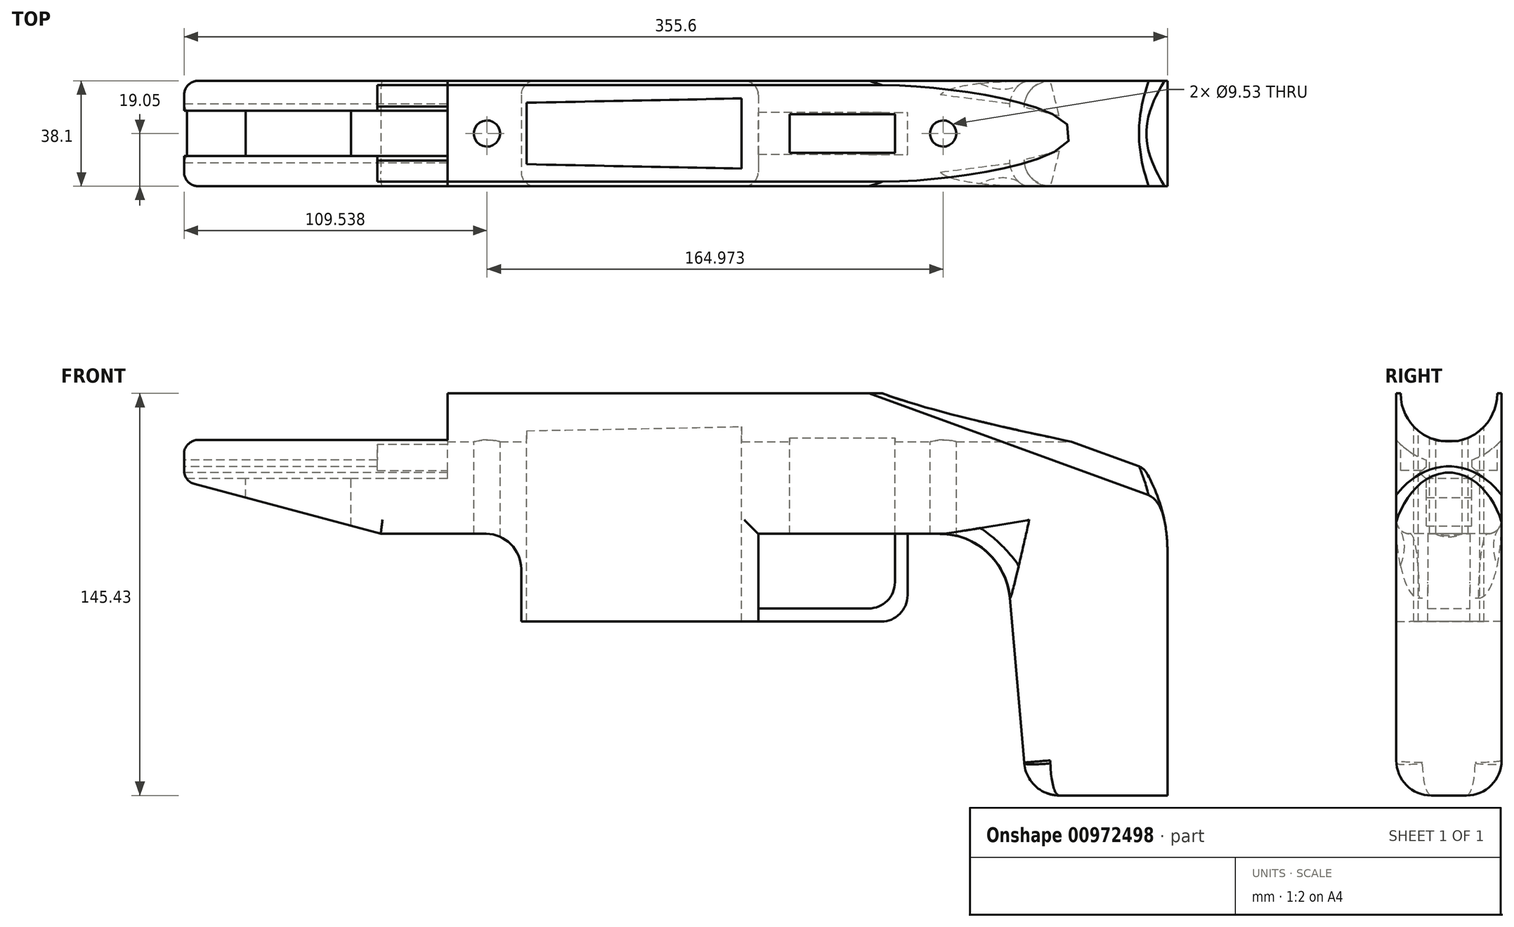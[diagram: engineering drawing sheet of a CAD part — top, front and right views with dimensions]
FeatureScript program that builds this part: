
annotation { "Feature Type Name" : "Feature", "Feature Type Description" : "" }
export const myFeature = defineFeature(function(context is Context, id is Id, definition is map)
    precondition{}
    {
        {
            var Q0;
            Q0=qCreatedBy(makeId("Front.planeOp"),FACE);
            var sketch = newSketch(context, id + "F0", { "sketchPlane" : qUnion([Q0])});
            skLineSegment(sketch, "E0", {"start": v(177.8, -57.15) * mm, "end": v(177.8, -145.43) * mm});
            skLineSegment(sketch, "E1", {"start": v(177.8, -145.43) * mm, "end": v(127, -145.43) * mm});
            skLineSegment(sketch, "E2", {"start": v(127, -145.43) * mm, "end": v(118.72, -50.8) * mm});
            skLineSegment(sketch, "E3", {"start": v(118.72, -50.8) * mm, "end": v(29.82, -50.8) * mm});
            skLineSegment(sketch, "E4", {"start": v(29.82, -50.8) * mm, "end": v(29.82, -82.55) * mm});
            skLineSegment(sketch, "E5", {"start": v(29.82, -82.55) * mm, "end": v(-55.9, -82.55) * mm});
            skLineSegment(sketch, "E6", {"start": v(-55.9, -82.55) * mm, "end": v(-55.9, -50.8) * mm});
            skLineSegment(sketch, "E7", {"start": v(-55.9, -50.8) * mm, "end": v(-106.7, -50.8) * mm});
            skLineSegment(sketch, "E8", {"start": v(-106.7, -50.8) * mm, "end": v(-177.8, -31.75) * mm});
            skLineSegment(sketch, "E9", {"start": v(-177.8, -31.75) * mm, "end": v(-177.8, -9.53) * mm});
            skLineSegment(sketch, "E10", {"start": v(-107.95, -9.53) * mm, "end": v(-107.95, 0) * mm});
            skLineSegment(sketch, "E11", {"start": v(-107.95, 0) * mm, "end": v(120.65, 0) * mm});
            skLineSegment(sketch, "E12", {"start": v(-107.95, -9.53) * mm, "end": v(-177.8, -9.53) * mm});
            skArc(sketch, "E13", {"start": v(177.8, -57.15) * mm, "mid": v(161.06, -16.74) * mm, "end": v(120.65, 0) * mm});
            skLineSegment(sketch, "E14", {"start": v(0, 57.34) * mm, "end": v(0, -146.77) * mm, "construction": true});
            skSolve(sketch);
        }
        {
            var Q0;
            Q0=makeQuery(id+"F0.imprint","IMPRINT",FACE,{"disambiguationData":[TD([[makeQuery(id+"F0.imprint","IMPRINT",EDGE,{"derivedFrom":sQuery(id+"F0.wireOp",EDGE,"E0")}),-1.0]])]});
            extrude(context, id + "F1", {"entities" : qUnion([Q0]), "oppositeDirection" : true, "depth" : 19.05 * mm, "offsetDistance" : 25.4 * mm, "hasSecondDirection" : true, "secondDirectionOppositeDirection" : false, "secondDirectionDepth" : 19.05 * mm});
        }
        {
            var Q0;
            Q0=makeQuery(id+"F1.opExtrude","CAP_EDGE",EDGE,{"disambiguationData":[OSD([sQuery(id+"F0.wireOp",EDGE,"E2")])],"isStart":true});
            var Q1;
            Q1=makeQuery(id+"F1.opExtrude","CAP_EDGE",EDGE,{"disambiguationData":[OSD([sQuery(id+"F0.wireOp",EDGE,"E2")])],"isStart":false});
            fillet(context, id + "F2", {"entities" : qUnion([Q0, Q1]), "radius" : 9.52 * mm, "tangentPropagation" : true, "allowEdgeOverflow" : false});
        }
        {
            var Q0;
            Q0=makeQuery(id+"F1.opExtrude","CAP_EDGE",EDGE,{"disambiguationData":[OSD([sQuery(id+"F0.wireOp",EDGE,"E1")])],"isStart":false});
            fillet(context, id + "F3", {"entities" : qUnion([Q0]), "radius" : 12.7 * mm, "tangentPropagation" : true, "allowEdgeOverflow" : false});
        }
        {
            var Q0;
            Q0=makeQuery(id+"F1.opExtrude","SWEPT_EDGE",EDGE,{"disambiguationData":[OSD([sQuery(id+"F0.wireOp",EDGE,"E6"),sQuery(id+"F0.wireOp",EDGE,"E7")])]});
            fillet(context, id + "F4", {"entities" : qUnion([Q0]), "radius" : 12.7 * mm, "tangentPropagation" : true, "allowEdgeOverflow" : false});
        }
        {
            var Q0;
            Q0=makeQuery(id+"F1.opExtrude","CAP_EDGE",EDGE,{"disambiguationData":[OSD([sQuery(id+"F0.wireOp",EDGE,"E3")])],"isStart":true});
            var Q1;
            Q1=makeQuery(id+"F1.opExtrude","CAP_EDGE",EDGE,{"disambiguationData":[OSD([sQuery(id+"F0.wireOp",EDGE,"E4")])],"isStart":true});
            var Q2;
            Q2=makeQuery(id+"F1.opExtrude","CAP_EDGE",EDGE,{"disambiguationData":[OSD([sQuery(id+"F0.wireOp",EDGE,"E6")])],"isStart":true});
            var Q3;
            Q3=makeQuery(id+"F1.opExtrude","CAP_EDGE",EDGE,{"disambiguationData":[OSD([sQuery(id+"F0.wireOp",EDGE,"E8")])],"isStart":true});
            var Q4;
            Q4=makeQuery(id+"F1.opExtrude","CAP_EDGE",EDGE,{"disambiguationData":[OSD([sQuery(id+"F0.wireOp",EDGE,"E3")])],"isStart":false});
            var Q5;
            Q5=makeQuery(id+"F1.opExtrude","CAP_EDGE",EDGE,{"disambiguationData":[OSD([sQuery(id+"F0.wireOp",EDGE,"E6")])],"isStart":false});
            var Q6;
            Q6=makeQuery(id+"F1.opExtrude","CAP_EDGE",EDGE,{"disambiguationData":[OSD([sQuery(id+"F0.wireOp",EDGE,"E8")])],"isStart":false});
            var Q7;
            Q7=makeQuery(id+"F1.opExtrude","CAP_EDGE",EDGE,{"disambiguationData":[OSD([sQuery(id+"F0.wireOp",EDGE,"E4")])],"isStart":false});
            fillet(context, id + "F5", {"entities" : qUnion([Q0, Q1, Q2, Q3, Q4, Q5, Q6, Q7]), "radius" : 5.08 * mm, "tangentPropagation" : true, "allowEdgeOverflow" : false});
        }
        {
            var Q0;
            Q0=makeQuery(id+"F1.opExtrude","CAP_EDGE",EDGE,{"disambiguationData":[OSD([sQuery(id+"F0.wireOp",EDGE,"E9")])],"isStart":false});
            fillet(context, id + "F6", {"entities" : qUnion([Q0]), "radius" : 5.08 * mm, "tangentPropagation" : true, "allowEdgeOverflow" : false});
        }
        {
            var Q0;
            Q0=qCreatedBy(makeId("Right.planeOp"),FACE);
            var sketch = newSketch(context, id + "F7", { "sketchPlane" : qUnion([Q0])});
            skCircle(sketch, "E15", {"center": v(0, 0) * mm, "radius": 17.46 * mm});
            skSolve(sketch);
        }
        {
            var Q0;
            Q0=makeQuery(id+"F7.imprint","IMPRINT",FACE,{"disambiguationData":[TD([[makeQuery(id+"F7.imprint","IMPRINT",EDGE,{"derivedFrom":sQuery(id+"F7.wireOp",EDGE,"E15")}),1.0]])]});
            extrude(context, id + "F8", {"entities" : qUnion([Q0]), "operationType" : NewBodyOperationType.REMOVE, "endBound" : BoundingType.THROUGH_ALL, "oppositeDirection" : true, "depth" : 25.4 * mm, "offsetDistance" : 25.4 * mm, "hasSecondDirection" : true, "secondDirectionBound" : SecondDirectionBoundingType.THROUGH_ALL, "secondDirectionOppositeDirection" : false, "secondDirectionDepth" : 25.4 * mm});
        }
        {
            var Q0;
            Q0=makeQuery(id+"F1.opExtrude","SWEPT_FACE",FACE,{"disambiguationData":[OSD([sQuery(id+"F0.wireOp",EDGE,"E9")])]});
            var sketch = newSketch(context, id + "F9", { "sketchPlane" : qUnion([Q0])});
            skLineSegment(sketch, "E16", {"start": v(0, 0) * mm, "end": v(0, -58.85) * mm, "construction": true});
            skPoint(sketch, "E16.endSnap0", {"position": v(0, -27.85) * mm});
            skLineSegment(sketch, "E17", {"start": v(-8.2, -24.04) * mm, "end": v(-8.2, -26.54) * mm});
            skLineSegment(sketch, "E18", {"start": v(-8.2, -26.54) * mm, "end": v(-10.67, -28.7) * mm});
            skLineSegment(sketch, "E19", {"start": v(-10.67, -28.7) * mm, "end": v(-8.2, -30.86) * mm});
            skLineSegment(sketch, "E20", {"start": v(-8.2, -30.86) * mm, "end": v(8.2, -30.86) * mm});
            skLineSegment(sketch, "E21", {"start": v(8.2, -30.86) * mm, "end": v(10.67, -28.7) * mm});
            skLineSegment(sketch, "E22", {"start": v(10.67, -28.7) * mm, "end": v(8.2, -26.54) * mm});
            skLineSegment(sketch, "E23", {"start": v(8.2, -26.54) * mm, "end": v(8.2, -24.04) * mm});
            skLineSegment(sketch, "E24", {"start": v(-10.67, -28.7) * mm, "end": v(10.67, -28.7) * mm, "construction": true});
            skArc(sketch, "E25", {"start": v(8.2, -24.04) * mm, "mid": v(0, 25.4) * mm, "end": v(-8.2, -24.04) * mm});
            skPoint(sketch, "E26.orphan", {"position": v(-8.2, -10.48) * mm});
            skPoint(sketch, "E27.orphan", {"position": v(8.2, -10.48) * mm});
            skSolve(sketch);
        }
        {
            var Q0;
            {var subQ11=sQuery(id+"F9.wireOp",EDGE,"E17");Q0=makeQuery(id+"F9.imprint","IMPRINT",FACE,{"disambiguationData":[TD([[makeQuery(id+"F9.imprint","IMPRINT",EDGE,{"derivedFrom":subQ11}),1.0]])]});}
            var Q1;
            {var subQ1=sQuery(id+"F0.wireOp",EDGE,"E9");var subQ2=makeQuery(id+"F1.opExtrude","SWEPT_FACE",FACE,{"disambiguationData":[OSD([subQ1])]});var subQ7=makeQuery(id+"F8.boolean.opBoolean","INTERSECT",EDGE,{"derivedFrom":[subQ2,makeQuery(id+"F8.opExtrude","SWEPT_FACE",FACE,{"disambiguationData":[OSD([sQuery(id+"F7.wireOp",EDGE,"E15")])]})]});Q1=makeQuery(id+"F9.imprint","IMPRINT",FACE,{"disambiguationData":[TD([[makeQuery(id+"F9.imprint","IMPRINT",EDGE,{"derivedFrom":subQ7}),-1.0]])]});}
            var Q2;
            {var subQ0=sQuery(id+"F0.wireOp",EDGE,"E12");var subQ1=sQuery(id+"F0.wireOp",EDGE,"E11");var subQ2=sQuery(id+"F0.wireOp",EDGE,"E10");Q2=makeQuery(id+"F8.boolean.opBoolean","SPLIT",FACE,{"disambiguationData":[TD([makeQuery(id+"F1.opExtrude","CAP_FACE",FACE,{"disambiguationData":[OSD([sQuery(id+"F0.wireOp",EDGE,"E0"),sQuery(id+"F0.wireOp",EDGE,"E1"),sQuery(id+"F0.wireOp",EDGE,"E2"),sQuery(id+"F0.wireOp",EDGE,"E3"),sQuery(id+"F0.wireOp",EDGE,"E4"),sQuery(id+"F0.wireOp",EDGE,"E5"),sQuery(id+"F0.wireOp",EDGE,"E6"),sQuery(id+"F0.wireOp",EDGE,"E7"),sQuery(id+"F0.wireOp",EDGE,"E8"),sQuery(id+"F0.wireOp",EDGE,"E9"),subQ2,subQ1,subQ0,sQuery(id+"F0.wireOp",EDGE,"E13")])],"isStart":true})])],"derivedFrom":makeQuery(id+"F1.opExtrude","SWEPT_FACE",FACE,{"disambiguationData":[OSD([subQ2])]})});}
            extrude(context, id + "F10", {"entities" : qUnion([Q0, Q1]), "operationType" : NewBodyOperationType.REMOVE, "endBound" : BoundingType.UP_TO_SURFACE, "oppositeDirection" : true, "depth" : 25.4 * mm, "endBoundEntityFace" : qUnion([Q2]), "offsetDistance" : 25.4 * mm});
        }
        {
            var Q0;
            Q0=qCreatedBy(makeId("Top.planeOp"),FACE);
            var sketch = newSketch(context, id + "F11", { "sketchPlane" : qUnion([Q0])});
            skPoint(sketch, "E28.0", {"position": v(-107.95, 0) * mm});
            skLineSegment(sketch, "E29", {"start": v(-107.95, 0) * mm, "end": v(-78.77, 0) * mm, "construction": true});
            skCircle(sketch, "E30", {"center": v(-68.26, 0) * mm, "radius": 4.76 * mm});
            skCircle(sketch, "E31", {"center": v(96.71, 0) * mm, "radius": 4.76 * mm});
            skSolve(sketch);
        }
        {
            var Q0;
            Q0=qSketchRegion(id+"F11",true);
            extrude(context, id + "F12", {"entities" : qUnion([Q0]), "operationType" : NewBodyOperationType.REMOVE, "endBound" : BoundingType.THROUGH_ALL, "oppositeDirection" : true, "depth" : 25.4 * mm, "offsetDistance" : 25.4 * mm});
        }
        {
            var Q0;
            Q0=makeQuery(id+"F1.opExtrude","SWEPT_EDGE",EDGE,{"disambiguationData":[OSD([sQuery(id+"F0.wireOp",EDGE,"E0"),sQuery(id+"F0.wireOp",EDGE,"E13")])]});
            cPlane(context, id + "F13", {"entities" : qUnion([Q0]), "cplaneType" : CPlaneType.LINE_ANGLE, "offset" : 25.4 * mm, "angle" : 110 * degree, "oppositeDirection" : true, "width" : 152.4 * mm, "height" : 152.4 * mm});
        }
        {
            var Q0;
            Q0=qCreatedBy(id+"F13.planeOp",FACE);
            var sketch = newSketch(context, id + "F14", { "sketchPlane" : qUnion([Q0])});
            skArc(sketch, "E32", {"start": v(19.05, 23.9) * mm, "mid": v(0, 32.5) * mm, "end": v(-19.05, 23.9) * mm});
            skLineSegment(sketch, "E33.0", {"start": v(19.05, 23.9) * mm, "end": v(19.05, 44.71) * mm});
            skLineSegment(sketch, "E34.0", {"start": v(-19.05, 23.9) * mm, "end": v(-19.05, 44.71) * mm});
            skLineSegment(sketch, "E35", {"start": v(19.05, 44.71) * mm, "end": v(-19.05, 44.71) * mm});
            skPoint(sketch, "E36.orphan", {"position": v(-19.05, 7.1) * mm});
            skPoint(sketch, "E37.0.end.orphan", {"position": v(19.05, 7.1) * mm});
            skSolve(sketch);
        }
        {
            var Q0;
            Q0=makeQuery(id+"F14.imprint","IMPRINT",FACE,{"disambiguationData":[TD([[makeQuery(id+"F14.imprint","IMPRINT",EDGE,{"derivedFrom":sQuery(id+"F14.wireOp",EDGE,"E32")}),-1.0]])]});
            extrude(context, id + "F15", {"entities" : qUnion([Q0]), "operationType" : NewBodyOperationType.REMOVE, "endBound" : BoundingType.THROUGH_ALL, "depth" : 25.4 * mm, "offsetDistance" : 25.4 * mm});
        }
        {
            var Q0;
            Q0=makeQuery(id+"F15.boolean.opBoolean","INTERSECT",EDGE,{"derivedFrom":[makeQuery(id+"F1.opExtrude","SWEPT_FACE",FACE,{"disambiguationData":[OSD([sQuery(id+"F0.wireOp",EDGE,"E13")])]}),makeQuery(id+"F15.opExtrude","SWEPT_FACE",FACE,{"disambiguationData":[OSD([sQuery(id+"F14.wireOp",EDGE,"E32")])]})]});
            fillet(context, id + "F16", {"entities" : qUnion([Q0]), "radius" : 5.08 * mm, "tangentPropagation" : true, "allowEdgeOverflow" : false});
        }
        {
            var Q0;
            Q0=qCreatedBy(makeId("Top.planeOp"),FACE);
            var sketch = newSketch(context, id + "F17", { "sketchPlane" : qUnion([Q0])});
            skLineSegment(sketch, "E38.0", {"start": v(-107.95, 17.46) * mm, "end": v(-107.95, -17.46) * mm});
            skLineSegment(sketch, "E39.0", {"start": v(-107.95, 17.46) * mm, "end": v(-82.55, 17.46) * mm});
            skLineSegment(sketch, "E40.0", {"start": v(-82.55, -17.46) * mm, "end": v(-107.95, -17.46) * mm});
            skLineSegment(sketch, "E41", {"start": v(-82.55, 17.46) * mm, "end": v(-82.55, -17.46) * mm});
            skPoint(sketch, "E42.orphan", {"position": v(74.71, 17.46) * mm});
            skPoint(sketch, "E43.orphan", {"position": v(74.71, -17.46) * mm});
            skSolve(sketch);
        }
        {
            var Q0;
            Q0=makeQuery(id+"F17.imprint","IMPRINT",FACE,{"disambiguationData":[TD([[makeQuery(id+"F17.imprint","IMPRINT",EDGE,{"derivedFrom":sQuery(id+"F17.wireOp",EDGE,"E38.0")}),1.0]])]});
            extrude(context, id + "F18", {"entities" : qUnion([Q0]), "operationType" : NewBodyOperationType.REMOVE, "oppositeDirection" : true, "depth" : 27.94 * mm, "offsetDistance" : 25.4 * mm});
        }
        {
            var Q0;
            Q0=qCreatedBy(makeId("Top.planeOp"),FACE);
            var sketch = newSketch(context, id + "F19", { "sketchPlane" : qUnion([Q0])});
            skLineSegment(sketch, "E44.0", {"start": v(-177.8, 9.7) * mm, "end": v(-177.8, -9.7) * mm, "construction": true});
            skLineSegment(sketch, "E45.0", {"start": v(-107.95, 9.7) * mm, "end": v(-107.95, -9.7) * mm, "construction": true});
            skLineSegment(sketch, "E46.0", {"start": v(-107.95, 8.2) * mm, "end": v(-177.8, 8.2) * mm});
            skLineSegment(sketch, "E47.0", {"start": v(-107.95, -8.2) * mm, "end": v(-177.8, -8.2) * mm});
            skLineSegment(sketch, "E48", {"start": v(-117.48, -8.2) * mm, "end": v(-117.48, 8.2) * mm});
            skLineSegment(sketch, "E49", {"start": v(-155.58, -8.2) * mm, "end": v(-155.58, 8.2) * mm});
            skSolve(sketch);
        }
        {
            var Q0;
            {var subQ0=sQuery(id+"F19.wireOp",EDGE,"E48");Q0=makeQuery(id+"F19.imprint","IMPRINT",FACE,{"disambiguationData":[TD([[makeQuery(id+"F19.imprint","IMPRINT",EDGE,{"derivedFrom":subQ0}),1.0]])]});}
            extrude(context, id + "F20", {"entities" : qUnion([Q0]), "operationType" : NewBodyOperationType.REMOVE, "endBound" : BoundingType.THROUGH_ALL, "oppositeDirection" : true, "depth" : 25.4 * mm, "offsetDistance" : 25.4 * mm});
        }
        {
            var Q0;
            Q0=qCreatedBy(makeId("Top.planeOp"),FACE);
            var sketch = newSketch(context, id + "F21", { "sketchPlane" : qUnion([Q0])});
            skLineSegment(sketch, "E50", {"start": v(-76.99, 0) * mm, "end": v(75.98, 0) * mm, "construction": true});
            skLineSegment(sketch, "E51", {"start": v(-53.98, 11.11) * mm, "end": v(-53.98, -11.11) * mm});
            skLineSegment(sketch, "E52", {"start": v(-53.98, -11.11) * mm, "end": v(23.83, -12.7) * mm});
            skLineSegment(sketch, "E53", {"start": v(23.83, -12.7) * mm, "end": v(23.83, 12.7) * mm});
            skLineSegment(sketch, "E54", {"start": v(23.83, 12.7) * mm, "end": v(-53.98, 11.11) * mm});
            skSolve(sketch);
        }
        {
            var Q0;
            Q0=makeQuery(id+"F21.imprint","IMPRINT",FACE,{"disambiguationData":[TD([[makeQuery(id+"F21.imprint","IMPRINT",EDGE,{"derivedFrom":sQuery(id+"F21.wireOp",EDGE,"E51")}),1.0]])]});
            extrude(context, id + "F22", {"entities" : qUnion([Q0]), "operationType" : NewBodyOperationType.REMOVE, "endBound" : BoundingType.THROUGH_ALL, "oppositeDirection" : true, "depth" : 25.4 * mm, "offsetDistance" : 25.4 * mm});
        }
        {
            var Q0;
            Q0=qSketchRegion(id+"F9",true);
            var Q1;
            Q1=makeQuery(id+"F18.boolean.opBoolean","COPY",FACE,{"derivedFrom":makeQuery(id+"F18.opExtrude","SWEPT_FACE",FACE,{"disambiguationData":[OSD([sQuery(id+"F17.wireOp",EDGE,"E41")])]})});
            extrude(context, id + "F23", {"entities" : qUnion([Q0]), "operationType" : NewBodyOperationType.REMOVE, "endBound" : BoundingType.UP_TO_SURFACE, "oppositeDirection" : true, "depth" : 25.4 * mm, "endBoundEntityFace" : qUnion([Q1]), "offsetDistance" : 25.4 * mm});
        }
        {
            var Q0;
            Q0=qCreatedBy(makeId("Top.planeOp"),FACE);
            var sketch = newSketch(context, id + "F24", { "sketchPlane" : qUnion([Q0])});
            skLineSegment(sketch, "E55", {"start": v(70.26, 0) * mm, "end": v(-50.54, 0) * mm, "construction": true});
            skLineSegment(sketch, "E56", {"start": v(79.25, 6.99) * mm, "end": v(79.25, -6.99) * mm});
            skLineSegment(sketch, "E57", {"start": v(79.25, -6.98) * mm, "end": v(41.15, -6.98) * mm});
            skLineSegment(sketch, "E58", {"start": v(41.15, -6.98) * mm, "end": v(41.15, 6.98) * mm});
            skLineSegment(sketch, "E59", {"start": v(79.25, 6.99) * mm, "end": v(41.15, 6.99) * mm});
            skSolve(sketch);
        }
        {
            var Q0;
            Q0=makeQuery(id+"F24.imprint","IMPRINT",FACE,{"disambiguationData":[TD([[makeQuery(id+"F24.imprint","IMPRINT",EDGE,{"derivedFrom":sQuery(id+"F24.wireOp",EDGE,"E56")}),-1.0]])]});
            var Q1;
            Q1=makeQuery(id+"F1.opExtrude","SWEPT_FACE",FACE,{"disambiguationData":[OSD([sQuery(id+"F0.wireOp",EDGE,"E3")])]});
            extrude(context, id + "F25", {"entities" : qUnion([Q0]), "operationType" : NewBodyOperationType.REMOVE, "endBound" : BoundingType.UP_TO_SURFACE, "oppositeDirection" : true, "depth" : 25.4 * mm, "endBoundEntityFace" : qUnion([Q1]), "offsetDistance" : 25.4 * mm});
        }
        {
            var Q0;
            Q0=qCreatedBy(makeId("Front.planeOp"),FACE);
            var sketch = newSketch(context, id + "F26", { "sketchPlane" : qUnion([Q0])});
            skLineSegment(sketch, "E60.0", {"start": v(29.82, -50.8) * mm, "end": v(119.83, -50.8) * mm});
            skLineSegment(sketch, "E61.0", {"start": v(29.82, -82.55) * mm, "end": v(29.82, -50.8) * mm});
            skLineSegment(sketch, "E62", {"start": v(83.8, -50.8) * mm, "end": v(83.8, -82.55) * mm});
            skLineSegment(sketch, "E63", {"start": v(83.8, -82.55) * mm, "end": v(29.82, -82.55) * mm});
            skPoint(sketch, "E64.0", {"position": v(79.25, -50.8) * mm});
            skLineSegment(sketch, "E65", {"start": v(79.25, -50.8) * mm, "end": v(79.25, -77.79) * mm});
            skLineSegment(sketch, "E66", {"start": v(79.25, -77.79) * mm, "end": v(29.82, -77.79) * mm});
            skSolve(sketch);
        }
        {
            var Q0;
            {var subQ1=sQuery(id+"F26.wireOp",EDGE,"E62");Q0=makeQuery(id+"F26.imprint","IMPRINT",FACE,{"disambiguationData":[TD([[makeQuery(id+"F26.imprint","IMPRINT",EDGE,{"derivedFrom":subQ1}),-1.0]])]});}
            extrude(context, id + "F27", {"entities" : qUnion([Q0]), "operationType" : NewBodyOperationType.ADD, "depth" : 7.62 * mm, "offsetDistance" : 25.4 * mm, "hasSecondDirection" : true, "secondDirectionOppositeDirection" : true, "secondDirectionDepth" : 7.62 * mm});
        }
        {
            var Q0;
            Q0=makeQuery(id+"F27.opExtrude","SWEPT_EDGE",EDGE,{"disambiguationData":[OSD([sQuery(id+"F26.wireOp",EDGE,"E62"),sQuery(id+"F26.wireOp",EDGE,"E63")])]});
            var Q1;
            Q1=makeQuery(id+"F27.opExtrude","SWEPT_EDGE",EDGE,{"disambiguationData":[OSD([sQuery(id+"F26.wireOp",EDGE,"E60.0"),sQuery(id+"F26.wireOp",EDGE,"E62")])]});
            var Q2;
            Q2=makeQuery(id+"F27.opExtrude","SWEPT_EDGE",EDGE,{"disambiguationData":[OSD([sQuery(id+"F26.wireOp",EDGE,"E65"),sQuery(id+"F26.wireOp",EDGE,"E66")])]});
            var Q3;
            Q3=makeQuery(id+"F27.opExtrude","SWEPT_EDGE",EDGE,{"disambiguationData":[OSD([sQuery(id+"F26.wireOp",EDGE,"E61.0"),sQuery(id+"F26.wireOp",EDGE,"E66")])]});
            fillet(context, id + "F28", {"entities" : qUnion([Q0, Q1, Q2, Q3]), "radius" : 9.52 * mm, "tangentPropagation" : true, "allowEdgeOverflow" : false});
        }
        {
            var Q0;
            Q0=makeQuery(id+"F1.opExtrude","SWEPT_EDGE",EDGE,{"disambiguationData":[OSD([sQuery(id+"F0.wireOp",EDGE,"E2"),sQuery(id+"F0.wireOp",EDGE,"E3")])]});
            fillet(context, id + "F29", {"entities" : qUnion([Q0]), "radius" : 25.4 * mm, "tangentPropagation" : true, "allowEdgeOverflow" : false});
        }
    });
